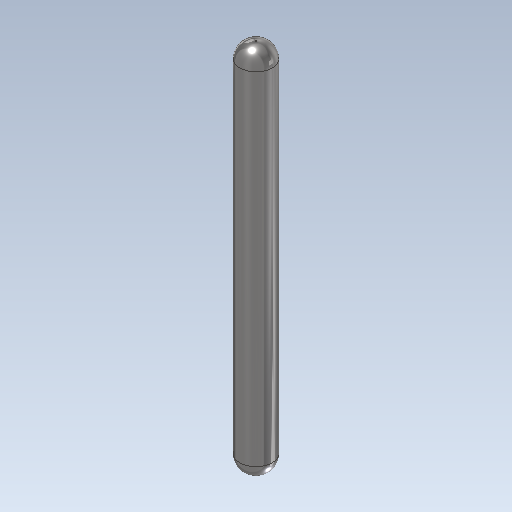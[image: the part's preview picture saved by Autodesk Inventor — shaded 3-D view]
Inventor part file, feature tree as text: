
AUTODESK INVENTOR PART (.ipt)
format: ipt  version: 2020 (Build 240168000, 168)  size: 99,328 bytes
history: native  units: in
note: dims shown in document units (in); Inventor stores cm internally (conversion verified against a paired STEP export)
features: extrude x1, fillet x1, sketch x1
ambient origin geometry x7: Origin, YZ Plane, XZ Plane, X Axis, Y Axis, Z Axis, Center Point
bodies: Solid1 (feature_tree)
feature tree (3):
  extrude  "ExtrusionMidplane1"  Depth=0.011in
  fillet  "Fillet1"  Radius=0.023in
  sketch  "Sketch1-<F>"  dims[d0=0.263in d1=0.0in d2=0.011in d3=0.023in]
